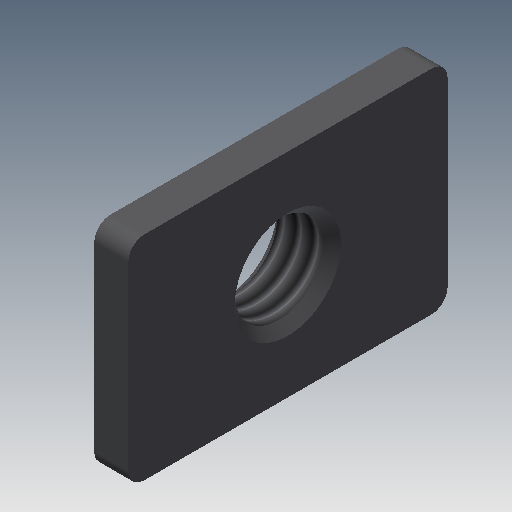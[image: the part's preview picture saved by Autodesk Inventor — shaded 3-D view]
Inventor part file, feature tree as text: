
AUTODESK INVENTOR PART (.ipt)
format: ipt  version: 2018 (Build 220112000, 112)  size: 135,168 bytes
history: native  units: mm
features: other x7, sketch x3, revolve x2, extrude x1, thread x1
ambient origin geometry x8: Origin, YZ Plane, XZ Plane, XY Plane, X Axis, Y Axis, Z Axis, Center Point
bodies: Solid1 (feature_tree)
feature tree (14):
  extrude  "Extrusion1"  TaperAngle=360.0deg  [1 undecoded]
  revolve  "Revolution1"  [1 undecoded]
  revolve  "Revolution2"  [1 undecoded]
  thread  "Thread1"  [1 undecoded]
  other  "dummy_XY"
  other  "dummy_YZ"
  other  "dummy_ZX"
  other  "dummy_X"
  other  "dummy_Y"
  other  "dummy_Z"
  other  "dummy_Center"
  sketch  "Sketch_1"  dims[d0=3.0mm d1=0.0mm d2=360.0deg]
  sketch  "Sketch_2"  dims[d3=360.0deg d4=2.134mm d5=0.0mm]
  sketch  "Sketch_3"
note: 4 required parameter values undecoded (feature->parameter linkage not recoverable at this tier; creation-order binding heuristic only, values carry confidence <= 0.55)